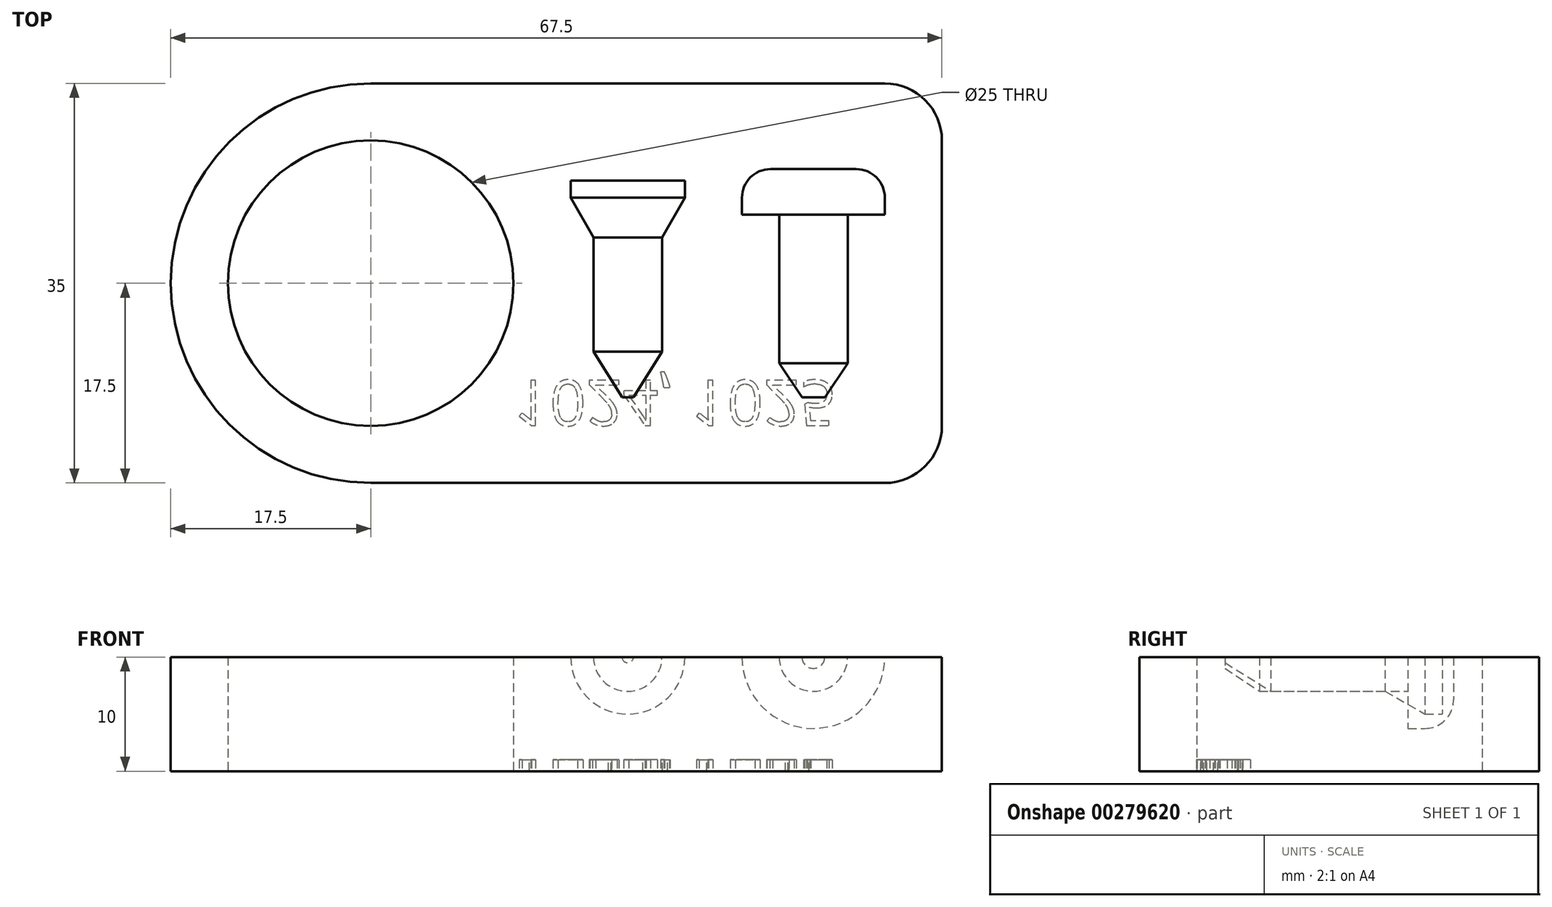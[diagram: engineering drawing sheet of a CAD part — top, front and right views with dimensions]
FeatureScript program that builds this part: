
annotation { "Feature Type Name" : "Feature", "Feature Type Description" : "" }
export const myFeature = defineFeature(function(context is Context, id is Id, definition is map)
    precondition{}
    {
        {
            var Q0;
            Q0=qCreatedBy(makeId("Top.planeOp"),FACE);
            var sketch = newSketch(context, id + "F0", { "sketchPlane" : qUnion([Q0])});
            skLineSegment(sketch, "E0.bottom", {"start": v(17.5, 0) * mm, "end": v(62.5, 0) * mm});
            skLineSegment(sketch, "E0.top", {"start": v(17.5, 35) * mm, "end": v(62.5, 35) * mm});
            skLineSegment(sketch, "E0.left", {"start": v(0, 17.5) * mm, "end": v(0, 17.5) * mm});
            skLineSegment(sketch, "E0.right", {"start": v(67.5, 5) * mm, "end": v(67.5, 30) * mm});
            skLineSegment(sketch, "E1.bottom", {"start": v(0, 0) * mm, "end": v(17.5, 0) * mm, "construction": true});
            skLineSegment(sketch, "E1.top", {"start": v(0, 17.5) * mm, "end": v(17.5, 17.5) * mm, "construction": true});
            skLineSegment(sketch, "E1.left", {"start": v(0, 0) * mm, "end": v(0, 17.5) * mm, "construction": true});
            skLineSegment(sketch, "E1.right", {"start": v(17.5, 0) * mm, "end": v(17.5, 17.5) * mm, "construction": true});
            skCircle(sketch, "E2", {"center": v(17.5, 17.5) * mm, "radius": 12.5 * mm});
            skPoint(sketch, "E3.visualSharp", {"position": v(0, 0) * mm});
            skArc(sketch, "E3.filletArc", {"start": v(0, 17.5) * mm, "mid": v(5.13, 5.13) * mm, "end": v(17.5, 0) * mm});
            skPoint(sketch, "E4.visualSharp", {"position": v(0, 35) * mm});
            skArc(sketch, "E4.filletArc", {"start": v(17.5, 35) * mm, "mid": v(5.13, 29.87) * mm, "end": v(0, 17.5) * mm});
            skPoint(sketch, "E5.visualSharp", {"position": v(67.5, 35) * mm});
            skArc(sketch, "E5.filletArc", {"start": v(67.5, 30) * mm, "mid": v(66.04, 33.54) * mm, "end": v(62.5, 35) * mm});
            skPoint(sketch, "E6.visualSharp", {"position": v(67.5, 0) * mm});
            skArc(sketch, "E6.filletArc", {"start": v(62.5, 0) * mm, "mid": v(66.04, 1.46) * mm, "end": v(67.5, 5) * mm});
            skSolve(sketch);
        }
        {
            var Q0;
            Q0=makeQuery(id+"F0.imprint","IMPRINT",FACE,{"disambiguationData":[TD([[makeQuery(id+"F0.imprint","IMPRINT",EDGE,{"derivedFrom":sQuery(id+"F0.wireOp",EDGE,"E0.bottom")}),1.0]])]});
            extrude(context, id + "F1", {"entities" : qUnion([Q0]), "depth" : 10 * mm});
        }
        {
            var Q0;
            Q0=makeQuery(id+"F1.opExtrude","CAP_FACE",FACE,{"disambiguationData":[OSD([sQuery(id+"F0.wireOp",EDGE,"E0.bottom"),sQuery(id+"F0.wireOp",EDGE,"E0.top"),sQuery(id+"F0.wireOp",EDGE,"E0.right"),sQuery(id+"F0.wireOp",EDGE,"E2"),sQuery(id+"F0.wireOp",EDGE,"E3.filletArc"),sQuery(id+"F0.wireOp",EDGE,"E4.filletArc"),sQuery(id+"F0.wireOp",EDGE,"E5.filletArc"),sQuery(id+"F0.wireOp",EDGE,"E6.filletArc")])],"isStart":false});
            var sketch = newSketch(context, id + "F2", { "sketchPlane" : qUnion([Q0])});
            skLineSegment(sketch, "E7.bottom", {"start": v(0, 0) * mm, "end": v(40, 0) * mm, "construction": true});
            skLineSegment(sketch, "E7.top", {"start": v(0, 7.5) * mm, "end": v(40, 7.5) * mm, "construction": true});
            skLineSegment(sketch, "E7.left", {"start": v(0, 0) * mm, "end": v(0, 7.5) * mm, "construction": true});
            skLineSegment(sketch, "E7.right", {"start": v(40, 0) * mm, "end": v(40, 7.5) * mm, "construction": true});
            skLineSegment(sketch, "E8", {"start": v(40, 7.5) * mm, "end": v(40, 26.5) * mm});
            skLineSegment(sketch, "E9", {"start": v(40, 26.5) * mm, "end": v(45, 26.5) * mm});
            skLineSegment(sketch, "E10", {"start": v(45, 26.5) * mm, "end": v(45, 25) * mm});
            skLineSegment(sketch, "E11", {"start": v(40, 7.5) * mm, "end": v(40.5, 7.5) * mm});
            skLineSegment(sketch, "E12", {"start": v(40.5, 7.5) * mm, "end": v(40.5, 11.5) * mm, "construction": true});
            skLineSegment(sketch, "E13", {"start": v(40.5, 11.5) * mm, "end": v(43, 11.5) * mm, "construction": true});
            skLineSegment(sketch, "E14", {"start": v(40.5, 7.5) * mm, "end": v(43, 11.5) * mm});
            skLineSegment(sketch, "E15", {"start": v(43, 11.5) * mm, "end": v(43, 21.5) * mm});
            skLineSegment(sketch, "E16", {"start": v(43, 21.5) * mm, "end": v(45, 25) * mm});
            skLineSegment(sketch, "E17", {"start": v(40, 7.5) * mm, "end": v(56.25, 7.5) * mm, "construction": true});
            skLineSegment(sketch, "E18", {"start": v(56.25, 7.5) * mm, "end": v(57.25, 7.5) * mm});
            skLineSegment(sketch, "E19", {"start": v(56.25, 7.5) * mm, "end": v(56.25, 23.5) * mm});
            skLineSegment(sketch, "E20.bottom", {"start": v(59.25, 23.5) * mm, "end": v(62.5, 23.5) * mm});
            skLineSegment(sketch, "E20.top", {"start": v(56.25, 27.5) * mm, "end": v(60, 27.5) * mm});
            skLineSegment(sketch, "E20.left", {"start": v(56.25, 23.5) * mm, "end": v(56.25, 27.5) * mm});
            skLineSegment(sketch, "E20.right", {"start": v(62.5, 23.5) * mm, "end": v(62.5, 25) * mm});
            skPoint(sketch, "E21.visualSharp", {"position": v(62.5, 27.5) * mm});
            skArc(sketch, "E21.filletArc", {"start": v(62.5, 25) * mm, "mid": v(61.77, 26.77) * mm, "end": v(60, 27.5) * mm});
            skLineSegment(sketch, "E22", {"start": v(59.25, 23.5) * mm, "end": v(59.25, 10.5) * mm});
            skLineSegment(sketch, "E23", {"start": v(59.25, 10.5) * mm, "end": v(57.25, 7.5) * mm});
            skSolve(sketch);
        }
        {
            var Q0;
            Q0=makeQuery(id+"F2.imprint","IMPRINT",FACE,{"disambiguationData":[TD([[makeQuery(id+"F2.imprint","IMPRINT",EDGE,{"derivedFrom":sQuery(id+"F2.wireOp",EDGE,"E8")}),-1.0]])]});
            var Q1;
            Q1=sQuery(id+"F2.wireOp",EDGE,"E8");
            revolve(context, id + "F3", {"operationType" : NewBodyOperationType.REMOVE, "entities" : qUnion([Q0]), "axis" : qUnion([Q1]), "revolveType" : RevolveType.FULL, "oppositeDirection" : true});
        }
        {
            var Q0;
            Q0=makeQuery(id+"F2.imprint","IMPRINT",FACE,{"disambiguationData":[TD([[makeQuery(id+"F2.imprint","IMPRINT",EDGE,{"derivedFrom":sQuery(id+"F2.wireOp",EDGE,"E18")}),1.0]])]});
            var Q1;
            Q1=sQuery(id+"F2.wireOp",EDGE,"E19");
            revolve(context, id + "F4", {"operationType" : NewBodyOperationType.REMOVE, "entities" : qUnion([Q0]), "axis" : qUnion([Q1]), "revolveType" : RevolveType.FULL, "oppositeDirection" : true});
        }
        {
            var Q0;
            Q0=makeQuery(id+"F1.opExtrude","CAP_FACE",FACE,{"disambiguationData":[OSD([sQuery(id+"F0.wireOp",EDGE,"E0.bottom"),sQuery(id+"F0.wireOp",EDGE,"E0.top"),sQuery(id+"F0.wireOp",EDGE,"E0.right"),sQuery(id+"F0.wireOp",EDGE,"E2"),sQuery(id+"F0.wireOp",EDGE,"E3.filletArc"),sQuery(id+"F0.wireOp",EDGE,"E4.filletArc"),sQuery(id+"F0.wireOp",EDGE,"E5.filletArc"),sQuery(id+"F0.wireOp",EDGE,"E6.filletArc")])],"isStart":true});
            var sketch = newSketch(context, id + "F5", { "sketchPlane" : qUnion([Q0])});
            skLineSegment(sketch, "E24.bottom", {"start": v(0, 0) * mm, "end": v(30, 0) * mm, "construction": true});
            skLineSegment(sketch, "E24.top", {"start": v(0, -5) * mm, "end": v(30, -5) * mm, "construction": true});
            skLineSegment(sketch, "E24.left", {"start": v(0, 0) * mm, "end": v(0, -5) * mm, "construction": true});
            skLineSegment(sketch, "E24.right", {"start": v(30, 0) * mm, "end": v(30, -5) * mm, "construction": true});
            skText(sketch, "E25", { "text": "1024, 1025", "fontName": "OpenSans-Regular.ttf"});
            const initialGuessF5  = {"E25": [0.03, -0.009, 1, 0, 0.004]};
            skSetInitialGuess(sketch, initialGuessF5);
            skSolve(sketch);
        }
        {
            var Q0;
            Q0 = qSketchRegion(id + "F5", true);
            extrude(context, id + "F6", {"entities" : qUnion([Q0]), "operationType" : NewBodyOperationType.REMOVE, "oppositeDirection" : true, "depth" : 1 * mm});
        }
    });
